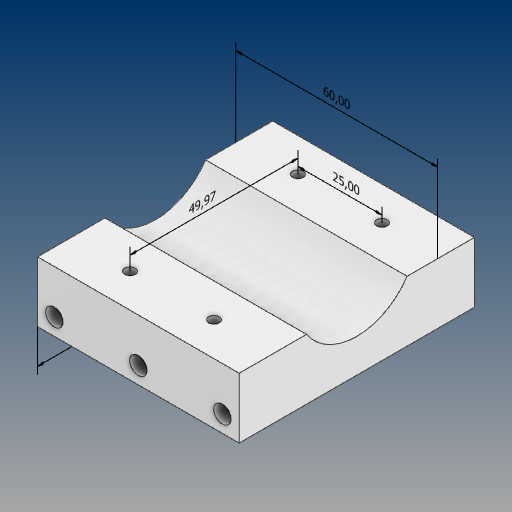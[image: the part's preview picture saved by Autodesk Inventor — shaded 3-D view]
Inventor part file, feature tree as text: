
AUTODESK INVENTOR PART (.ipt)
format: ipt  version: 2021 (Build 250183000, 183)  size: 167,936 bytes
history: native  units: mm
features: projected_geometry x6, other x5, sketch x4, extrude x2, hole x2
ambient origin geometry x8: Origin, YZ Plane, XZ Plane, XY Plane, X Axis, Y Axis, Z Axis, Center Point
bodies: Solid1 (feature_tree)
feature tree (19):
  other  "Annotations"
  extrude  "Extrusion1"  Depth=70.0mm
  hole  "Hole1"  [1 undecoded]
  extrude  "Extrusion2"  Depth=60.0mm
  hole  "Hole2"  [1 undecoded]
  sketch  "Sketch1"  dims[d0=60.0mm d1=70.0mm]
  sketch  "Sketch2"  dims[d2=18.0mm d3=0.0mm d4=5.0mm]
  projected_geometry  "Projected Loop1"
  sketch  "Sketch3"  dims[d6=5.0mm]
  projected_geometry  "Projected Loop2"
  projected_geometry  "Projected Loop3"
  sketch  "Sketch4"  dims[d7=5.2mm d8=6.0mm d9=4.0mm d10=2.0mm d11=90.0deg d12=8.0mm d13=20.594885mm d14=36.0mm d15=10.0mm d16=0.0mm d17=0.0mm d18=3.2mm d19=6.0mm d20=4.0mm d21=2.0mm d22=90.0deg d23=8.0mm d24=20.594885mm d25=64.081708mm d26=64.516985mm d27=25.0mm d28=64.55023mm d29=64.317167mm d30=49.96663mm d31=0.0mm d32=10.0mm d33=70.0mm d34=8.428356mm d35=5.760062mm d36=60.0mm]
  projected_geometry  "Projected Loop4"
  projected_geometry  "Projected Loop5"
  projected_geometry  "Projected Loop6"
  other  "Linear Dimension 1"
  other  "Linear Dimension 2"
  other  "Linear Dimension 3"
  other  "Linear Dimension 4"
note: 2 required parameter values undecoded (feature->parameter linkage not recoverable at this tier; creation-order binding heuristic only, values carry confidence <= 0.55)
